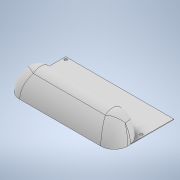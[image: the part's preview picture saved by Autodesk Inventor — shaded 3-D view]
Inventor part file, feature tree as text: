
AUTODESK INVENTOR PART (.ipt)
format: ipt  version: 2021 (Build 250183000, 183)  size: 187,904 bytes
history: native  units: mm
features: extrude x3, sketch x3, fillet x2
ambient origin geometry x8: Origin, YZ Plane, XZ Plane, XY Plane, X Axis, Y Axis, Z Axis, Center Point
bodies: Solid1 (feature_tree)
feature tree (8):
  extrude  "Extrusion1"  Depth=60.0mm
  extrude  "Extrusion4"  Depth=200.0mm
  fillet  "Fillet1"  Radius=50.0mm
  fillet  "Fillet2"  Radius=50.0mm
  extrude  "Extrusion5"  Depth=20.0mm
  sketch  "Sketch1"  dims[d0=200.0mm d1=60.0mm]
  sketch  "Sketch4"  dims[d2=1.0mm d3=0.0mm d12=200.0mm d13=50.0mm d14=50.0mm d15=0.0mm]
  sketch  "Sketch5"  dims[d16=50.0mm d17=20.0mm d18=5.0mm d19=5.0mm d20=5.0mm d21=5.0mm d22=1.0mm d23=0.0mm]
